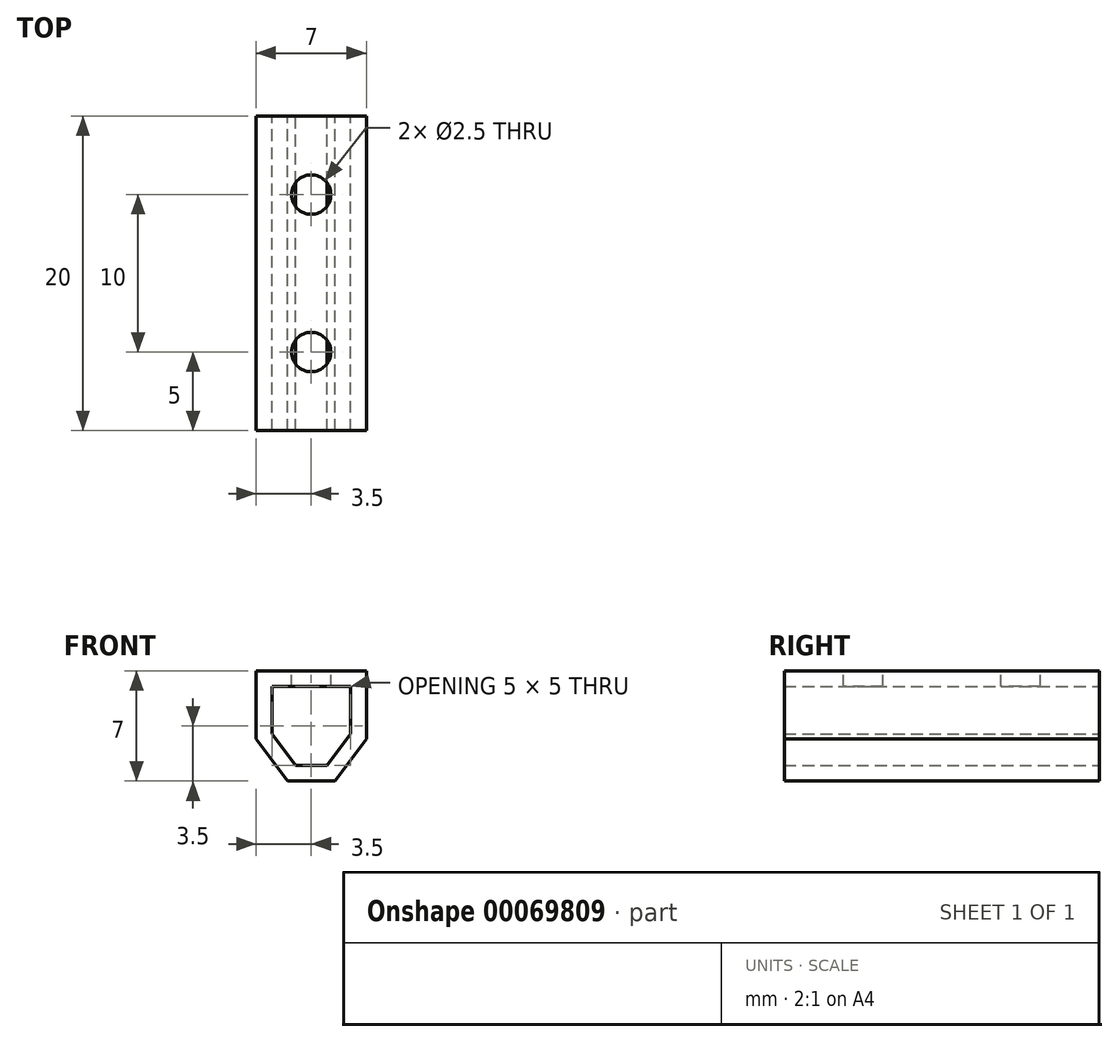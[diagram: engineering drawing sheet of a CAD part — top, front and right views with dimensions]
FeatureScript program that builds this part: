
annotation { "Feature Type Name" : "Feature", "Feature Type Description" : "" }
export const myFeature = defineFeature(function(context is Context, id is Id, definition is map)
    precondition{}
    {
        {
            var Q0;
            Q0=qCreatedBy(makeId("Front.planeOp"),FACE);
            var sketch = newSketch(context, id + "F0", { "sketchPlane" : qUnion([Q0])});
            skLineSegment(sketch, "E0", {"start": v(0, 0) * mm, "end": v(0, 5) * mm, "construction": true});
            skLineSegment(sketch, "E1", {"start": v(0, 5) * mm, "end": v(2.5, 5) * mm});
            skLineSegment(sketch, "E2", {"start": v(2.5, 5) * mm, "end": v(2.5, 2) * mm});
            skLineSegment(sketch, "E3", {"start": v(2.5, 2) * mm, "end": v(1, 0) * mm});
            skLineSegment(sketch, "E4", {"start": v(1, 0) * mm, "end": v(0, 0) * mm});
            skLineSegment(sketch, "E5.MirrorCS", {"start": v(-2.5, 2) * mm, "end": v(-1, 0) * mm});
            skLineSegment(sketch, "E6.MirrorCS", {"start": v(-1, 0) * mm, "end": v(0, 0) * mm});
            skLineSegment(sketch, "E7.MirrorCS", {"start": v(0, 5) * mm, "end": v(-2.5, 5) * mm});
            skLineSegment(sketch, "E8.MirrorCS", {"start": v(-2.5, 5) * mm, "end": v(-2.5, 2) * mm});
            skLineSegment(sketch, "E9.0", {"start": v(-3.5, 6) * mm, "end": v(3.5, 6) * mm});
            skLineSegment(sketch, "E9.1", {"start": v(3.5, 6) * mm, "end": v(3.5, 1.67) * mm});
            skLineSegment(sketch, "E9.2", {"start": v(-3.5, 6) * mm, "end": v(-3.5, 6) * mm});
            skLineSegment(sketch, "E9.3", {"start": v(3.5, 1.67) * mm, "end": v(1.5, -1) * mm});
            skLineSegment(sketch, "E9.4", {"start": v(-3.5, 6) * mm, "end": v(-3.5, 1.67) * mm});
            skLineSegment(sketch, "E9.5", {"start": v(-3.5, 1.67) * mm, "end": v(-1.5, -1) * mm});
            skLineSegment(sketch, "E9.6", {"start": v(-1.5, -1) * mm, "end": v(0, -1) * mm});
            skLineSegment(sketch, "E9.7", {"start": v(1.5, -1) * mm, "end": v(0, -1) * mm});
            skSolve(sketch);
        }
        {
            var Q0;
            Q0=makeQuery(id+"F0.imprint","IMPRINT",FACE,{"disambiguationData":[TD([[makeQuery(id+"F0.imprint","IMPRINT",EDGE,{"derivedFrom":sQuery(id+"F0.wireOp",EDGE,"E1")}),1.0]])]});
            extrude(context, id + "F1", {"entities" : qUnion([Q0]), "depth" : 10 * mm});
        }
        {
            var Q0;
            Q0=makeQuery(id+"F1.opExtrude","SWEPT_FACE",FACE,{"disambiguationData":[OSD([sQuery(id+"F0.wireOp",EDGE,"E9.0")])]});
            var sketch = newSketch(context, id + "F2", { "sketchPlane" : qUnion([Q0])});
            skLineSegment(sketch, "E10", {"start": v(-3.5, -5) * mm, "end": v(3.5, -5) * mm, "construction": true});
            skLineSegment(sketch, "E11", {"start": v(0, 0) * mm, "end": v(0, -10) * mm, "construction": true});
            skCircle(sketch, "E12", {"center": v(0, -5) * mm, "radius": 1.25 * mm});
            skSolve(sketch);
        }
        {
            var Q0;
            Q0=makeQuery(id+"F2.imprint","IMPRINT",FACE,{"disambiguationData":[TD([[makeQuery(id+"F2.imprint","IMPRINT",EDGE,{"derivedFrom":sQuery(id+"F2.wireOp",EDGE,"E12")}),1.0]])]});
            extrude(context, id + "F3", {"entities" : qUnion([Q0]), "operationType" : NewBodyOperationType.REMOVE, "endBound" : BoundingType.UP_TO_NEXT, "oppositeDirection" : true, "depth" : 25 * mm});
        }
        {
            var Q0;
            Q0=makeQuery(id+"F1.opExtrude","SWEPT_BODY",BODY,{"disambiguationData":[OSD([sQuery(id+"F0.wireOp",EDGE,"E1"),sQuery(id+"F0.wireOp",EDGE,"E2"),sQuery(id+"F0.wireOp",EDGE,"E3"),sQuery(id+"F0.wireOp",EDGE,"E4"),sQuery(id+"F0.wireOp",EDGE,"E5.MirrorCS"),sQuery(id+"F0.wireOp",EDGE,"E6.MirrorCS"),sQuery(id+"F0.wireOp",EDGE,"E7.MirrorCS"),sQuery(id+"F0.wireOp",EDGE,"E8.MirrorCS"),sQuery(id+"F0.wireOp",EDGE,"E9.0"),sQuery(id+"F0.wireOp",EDGE,"E9.1"),sQuery(id+"F0.wireOp",EDGE,"E9.3"),sQuery(id+"F0.wireOp",EDGE,"E9.4"),sQuery(id+"F0.wireOp",EDGE,"E9.5"),sQuery(id+"F0.wireOp",EDGE,"E9.6"),sQuery(id+"F0.wireOp",EDGE,"E9.7")])]});
            var Q1;
            Q1=makeQuery(id+"F1.opExtrude","CAP_FACE",FACE,{"disambiguationData":[OSD([sQuery(id+"F0.wireOp",EDGE,"E1"),sQuery(id+"F0.wireOp",EDGE,"E2"),sQuery(id+"F0.wireOp",EDGE,"E3"),sQuery(id+"F0.wireOp",EDGE,"E4"),sQuery(id+"F0.wireOp",EDGE,"E5.MirrorCS"),sQuery(id+"F0.wireOp",EDGE,"E6.MirrorCS"),sQuery(id+"F0.wireOp",EDGE,"E7.MirrorCS"),sQuery(id+"F0.wireOp",EDGE,"E8.MirrorCS"),sQuery(id+"F0.wireOp",EDGE,"E9.0"),sQuery(id+"F0.wireOp",EDGE,"E9.1"),sQuery(id+"F0.wireOp",EDGE,"E9.3"),sQuery(id+"F0.wireOp",EDGE,"E9.4"),sQuery(id+"F0.wireOp",EDGE,"E9.5"),sQuery(id+"F0.wireOp",EDGE,"E9.6"),sQuery(id+"F0.wireOp",EDGE,"E9.7")])],"isStart":true});
            mirror(context, id + "F4", {"operationType" : NewBodyOperationType.ADD, "entities" : qUnion([Q0]), "mirrorPlane" : qUnion([Q1])});
        }
    });
